# Revit family: Haworth_AWood_Bench_FixedLegs_DoubleIntermediaryModule_EU_PRELIMINARY
name_source: partatom
category: Furniture
units: mm (PartAtom-declared; Revit-internal decimal feet)

## family parameters
Always vertical = Yes
Cut with Voids When Loaded = No
OmniClass Number = 23.40.70.14.64.11
OmniClass Title = Office Furniture
Room Calculation Point = No
Shared = No
Work Plane-Based = No

## types (8) — shared parameters
Actual Height = 73 cm
Assembly Code = E2020200
Description = Haworth - A_Wood - Fixed Legs - Double Intermediary Module
Flip Top Finish = Haworth _ Paint _ Metallic Silver
Leg Height = 70 cm
Manufacturer = Haworth
Model = AWB4LXXXX
Revision Number = 1
Size = Verify Final Dim.w/ Haworth
Trim Finish = Haworth _ Metal _ Structured White EC
URL = https://www.haworth.com
URL - Product = https://www.haworth.com
Warranty = http://www.haworth.com
Worksurface Depth = 160, 180, 200cm
Worksurface Width = 120, 140, 160, 180, 200cm

## per-type parameters (varying)
| type | Accessory Kit | Actual Depth | Actual Width | Central Rail | Depth | Flip Top Cable Outlet | Large | Medium | No Accessory Kit | Round Cable Outlet | Small | Tray Depth |
| 120 x 160 | No | 160 cm | 120 cm | No | 160 cm | No | No | No | Yes | No | Yes | 80 cm |
| 140 x 180 | No | 180 cm | 140 cm | Yes | 89 cm | No | No | Yes | Yes | No | No | 100 cm |
| 160 x 200 | No | 200 cm | 160 cm | Yes | 99 cm | No | Yes | No | No | Yes | No | 120 cm |
| 180 x 160 | No | 160 cm | 180 cm | No | 160 cm | No | No | No | Yes | No | Yes | 80 cm |
| 200 x 180 | No | 180 cm | 200 cm | Yes | 89 cm | No | No | Yes | Yes | No | No | 100 cm |
| 200 x 200 | Yes | 200 cm | 200 cm | Yes | 99 cm | Yes | Yes | No | No | No | No | 120 cm |
| 160 x 160 | Yes | 160 cm | 160 cm | No | 160 cm | Yes | No | No | No | No | Yes | 80 cm |
| 180 x 180 | No | 180 cm | 180 cm | Yes | 89 cm | No | No | Yes | Yes | No | No | 100 cm |

## geometry (parser evidence)
native form markers: Sweep x21
no freeform markers — native parametric forms only
